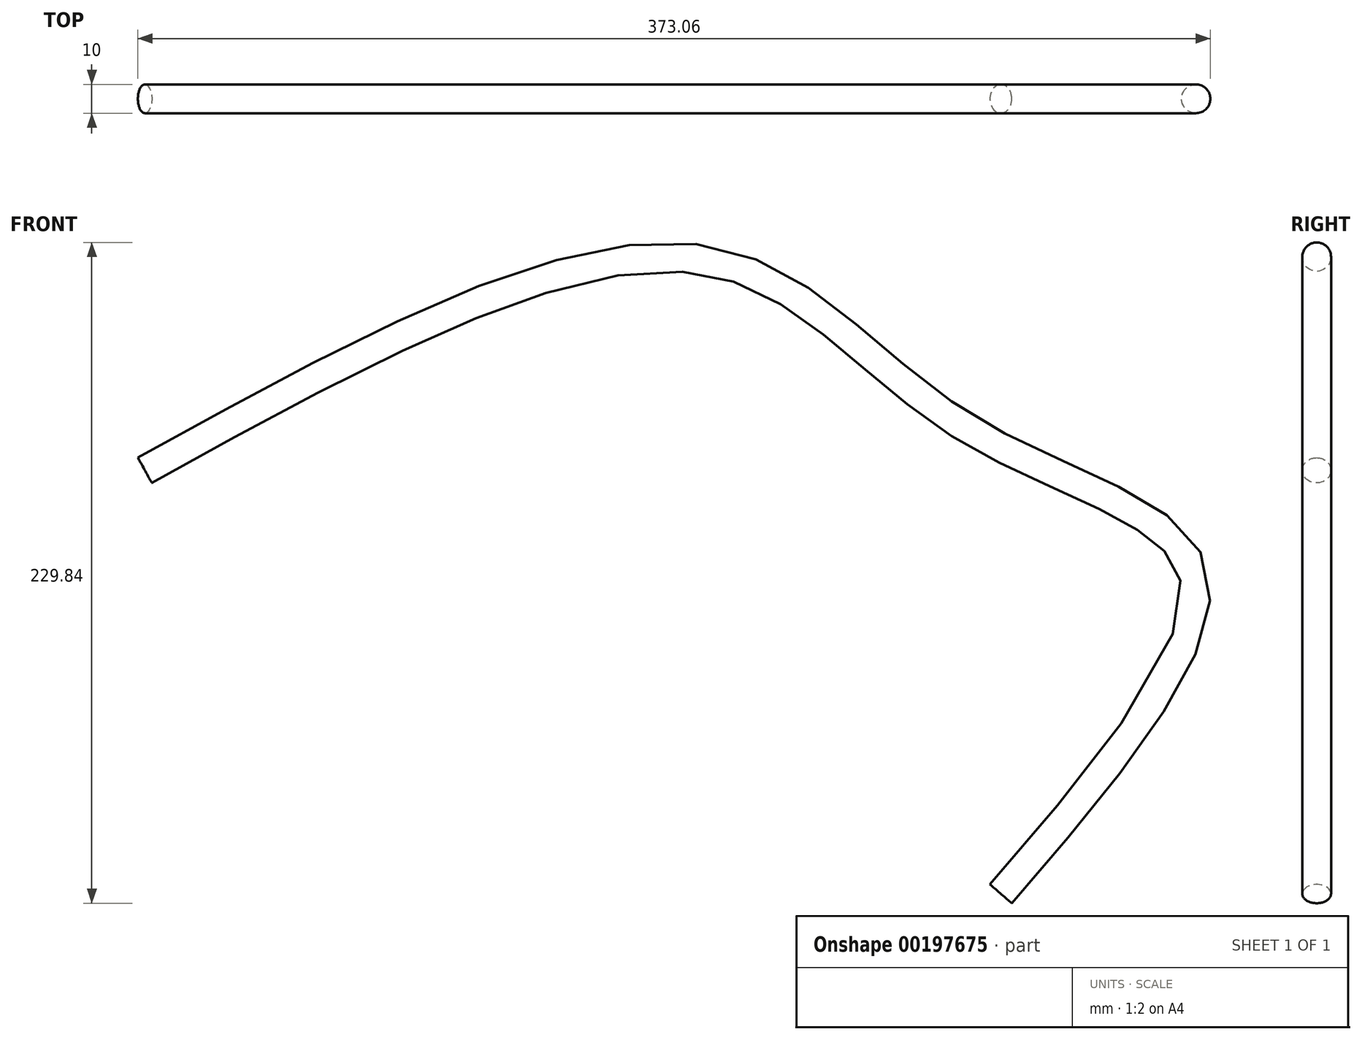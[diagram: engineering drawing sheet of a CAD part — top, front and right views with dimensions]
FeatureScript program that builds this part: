
annotation { "Feature Type Name" : "Feature", "Feature Type Description" : "" }
export const myFeature = defineFeature(function(context is Context, id is Id, definition is map)
    precondition{}
    {
        {
            var Q0;
            Q0=qCreatedBy(makeId("Front.planeOp"),FACE);
            var sketch = newSketch(context, id + "F0", { "sketchPlane" : qUnion([Q0])});
            skFitSpline(sketch, "E0", {"points": [v(0, 0) * mm, v(66.53, 113.13) * mm, v(-11.9, 161.9) * mm, v(-101.3, 220.33) * mm, v(-297.78, 147.32) * mm], "startDerivative": vector(453.23, 526.06) * mm, "endDerivative": vector(-702.96, -389.7) * mm});
            skFitSpline(sketch, "E1", {"points": [v(-223.84, 188.31) * mm, v(-309.66, 314.77) * mm, v(-433.05, 296.6) * mm, v(-544, 250.68) * mm], "startDerivative": vector(-197.62, 460.8) * mm, "endDerivative": vector(-331.97, -142.22) * mm});
            skSolve(sketch);
        }
        {
            var Q0;
            Q0=sQuery(id+"F0.wireOp",EDGE,"E0");
            var Q1;
            Q1=sQuery(id+"F0.wireOp",VERTEX,"E0.start");
            cPlane(context, id + "F1", {"entities" : qUnion([Q0, Q1]), "cplaneType" : CPlaneType.CURVE_POINT, "offset" : 25 * mm, "width" : 150 * mm, "height" : 150 * mm});
        }
        {
            var Q0;
            Q0=qCreatedBy(id+"F1.planeOp",FACE);
            var sketch = newSketch(context, id + "F2", { "sketchPlane" : qUnion([Q0])});
            skCircle(sketch, "E2", {"center": v(0, 0) * mm, "radius": 5 * mm});
            skSolve(sketch);
        }
        {
            var Q0;
            Q0=makeQuery(id+"F2.imprint","IMPRINT",FACE,{"disambiguationData":[TD([[makeQuery(id+"F2.imprint","IMPRINT",EDGE,{"derivedFrom":sQuery(id+"F2.wireOp",EDGE,"E2")}),1.0]])]});
            var Q1;
            Q1=sQuery(id+"F0.wireOp",EDGE,"E0");
            sweep(context, id + "F3", {"profiles" : qUnion([Q0]), "path" : qUnion([Q1])});
        }
    });
